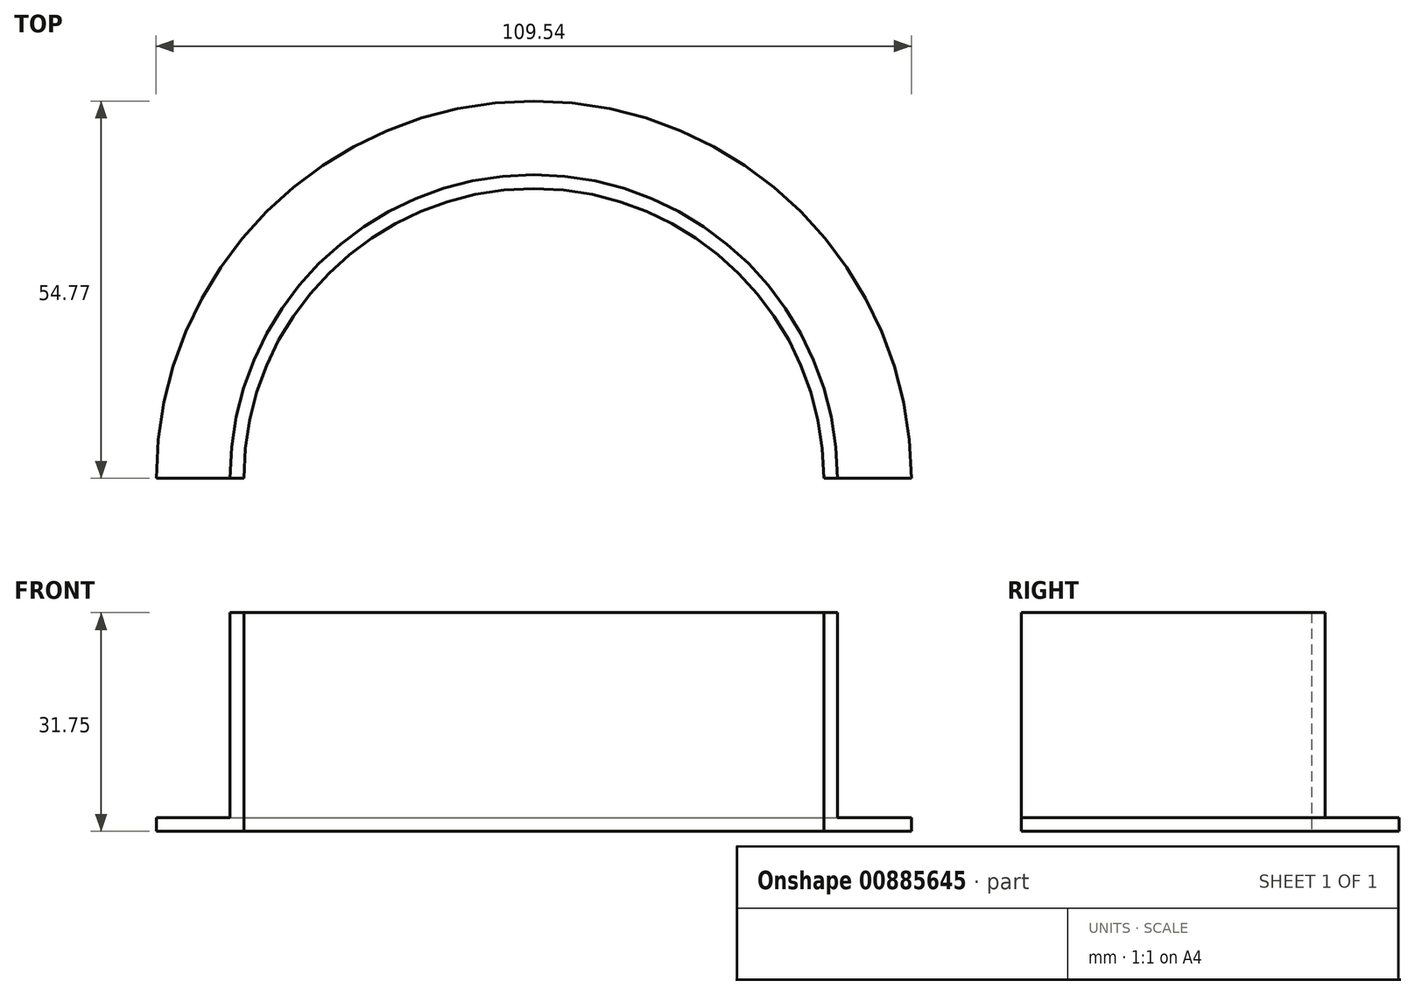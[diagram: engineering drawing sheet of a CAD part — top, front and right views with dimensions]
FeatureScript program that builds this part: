
annotation { "Feature Type Name" : "Feature", "Feature Type Description" : "" }
export const myFeature = defineFeature(function(context is Context, id is Id, definition is map)
    precondition{}
    {
        {
            var Q0;
            Q0=qCreatedBy(makeId("Front.planeOp"),FACE);
            var sketch = newSketch(context, id + "F0", { "sketchPlane" : qUnion([Q0])});
            skLineSegment(sketch, "E0", {"start": v(0, 0) * mm, "end": v(0, 96.17) * mm, "construction": true});
            skLineSegment(sketch, "E1", {"start": v(44.07, 31.75) * mm, "end": v(44.07, 2) * mm});
            skLineSegment(sketch, "E2", {"start": v(44.07, 2) * mm, "end": v(54.77, 2) * mm});
            skLineSegment(sketch, "E3", {"start": v(54.77, 2) * mm, "end": v(54.77, 0) * mm});
            skLineSegment(sketch, "E4", {"start": v(54.77, 0) * mm, "end": v(42.07, 0) * mm});
            skLineSegment(sketch, "E5", {"start": v(42.07, 0) * mm, "end": v(42.07, 31.75) * mm});
            skLineSegment(sketch, "E6", {"start": v(42.07, 31.75) * mm, "end": v(44.07, 31.75) * mm});
            skSolve(sketch);
        }
        {
            var Q0;
            Q0=makeQuery(id+"F0.imprint","IMPRINT",FACE,{"disambiguationData":[TD([[makeQuery(id+"F0.imprint","IMPRINT",EDGE,{"derivedFrom":sQuery(id+"F0.wireOp",EDGE,"E1")}),-1.0]])]});
            var Q1;
            Q1=sQuery(id+"F0.wireOp",EDGE,"E0");
            revolve(context, id + "F1", {"surfaceOperationType" : NewSurfaceOperationType.NEW, "entities" : qUnion([Q0]), "axis" : qUnion([Q1]), "revolveType" : RevolveType.ONE_DIRECTION, "angle" : 180 * degree});
        }
    });
